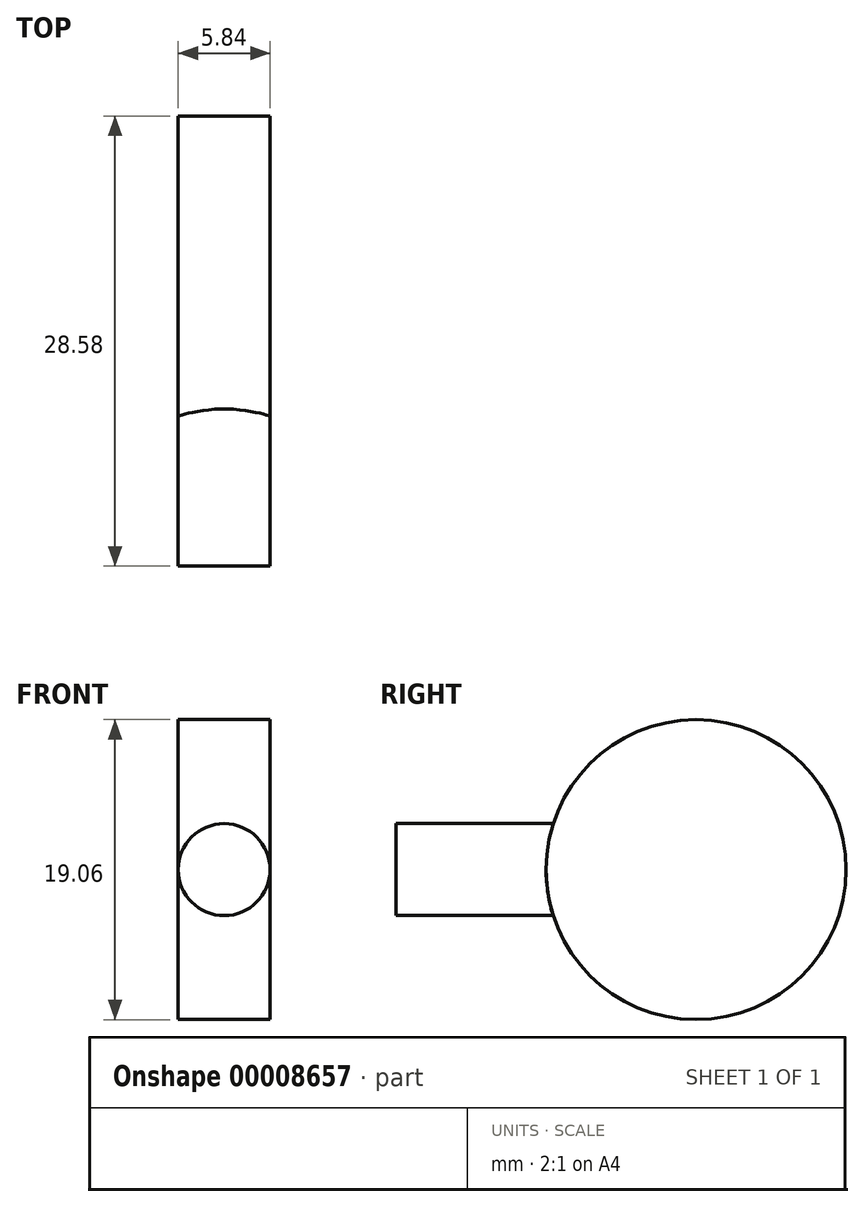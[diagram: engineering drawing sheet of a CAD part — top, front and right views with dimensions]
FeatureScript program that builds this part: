
annotation { "Feature Type Name" : "Feature", "Feature Type Description" : "" }
export const myFeature = defineFeature(function(context is Context, id is Id, definition is map)
    precondition{}
    {
        {
            var Q0;
            Q0=qCreatedBy(makeId("Front.planeOp"),FACE);
            var sketch = newSketch(context, id + "F0", { "sketchPlane" : qUnion([Q0])});
            skCircle(sketch, "E0", {"center": v(0, 0) * mm, "radius": 2.92 * mm});
            skSolve(sketch);
        }
        {
            var Q0;
            Q0 = qSketchRegion(id + "F0", true);
            extrude(context, id + "F1", {"entities" : qUnion([Q0]), "depth" : 19.05 * mm});
        }
        {
            var Q0;
            Q0=qCreatedBy(makeId("Right.planeOp"),FACE);
            var sketch = newSketch(context, id + "F2", { "sketchPlane" : qUnion([Q0])});
            skCircle(sketch, "E1", {"center": v(0, 0) * mm, "radius": 9.53 * mm});
            skSolve(sketch);
        }
        {
            var Q0;
            Q0 = qSketchRegion(id + "F2", true);
            extrude(context, id + "F3", {"entities" : qUnion([Q0]), "operationType" : NewBodyOperationType.ADD, "endBound" : BoundingType.SYMMETRIC, "depth" : 5.84 * mm});
        }
    });
